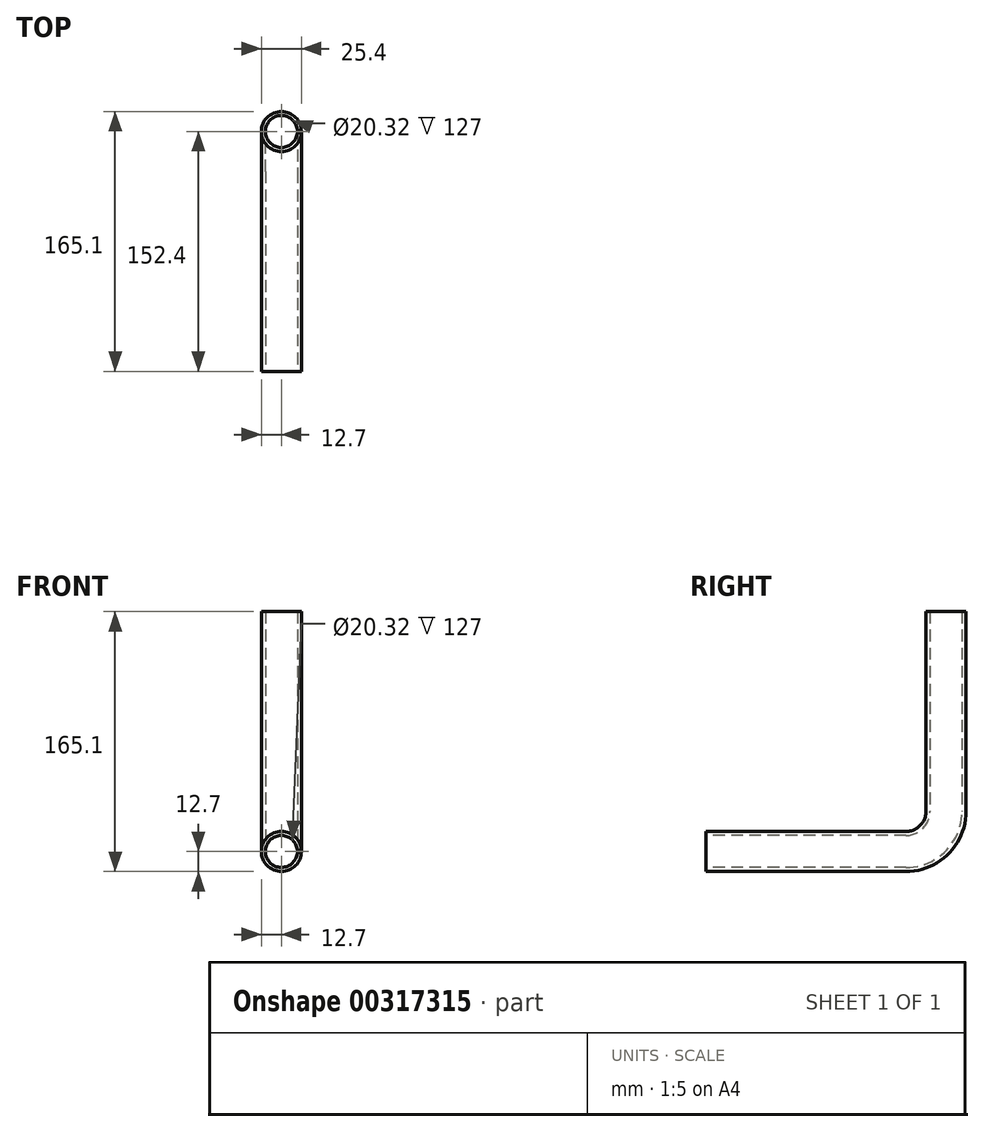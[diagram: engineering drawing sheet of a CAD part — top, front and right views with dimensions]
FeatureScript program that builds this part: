
annotation { "Feature Type Name" : "Feature", "Feature Type Description" : "" }
export const myFeature = defineFeature(function(context is Context, id is Id, definition is map)
    precondition{}
    {
        {
            var Q0;
            Q0=qCreatedBy(makeId("Right.planeOp"),FACE);
            var sketch = newSketch(context, id + "F0", { "sketchPlane" : qUnion([Q0])});
            skArc(sketch, "E0", {"start": v(-25.4, -152.4) * mm, "mid": v(-7.44, -144.96) * mm, "end": v(0, -127) * mm});
            skLineSegment(sketch, "E1", {"start": v(0, 0) * mm, "end": v(0, -127) * mm});
            skLineSegment(sketch, "E2", {"start": v(-25.4, -152.4) * mm, "end": v(-152.4, -152.4) * mm});
            skSolve(sketch);
        }
        {
            var Q0;
            Q0=qCreatedBy(makeId("Top.planeOp"),FACE);
            var sketch = newSketch(context, id + "F1", { "sketchPlane" : qUnion([Q0])});
            skCircle(sketch, "E3", {"center": v(0, 0) * mm, "radius": 12.7 * mm});
            skCircle(sketch, "E4", {"center": v(0, 0) * mm, "radius": 10.16 * mm});
            skSolve(sketch);
        }
        {
            var Q0;
            Q0=makeQuery(id+"F1.imprint","IMPRINT",FACE,{"disambiguationData":[TD([[makeQuery(id+"F1.imprint","IMPRINT",EDGE,{"derivedFrom":sQuery(id+"F1.wireOp",EDGE,"E3")}),1.0]])]});
            var Q1;
            Q1=sQuery(id+"F0.wireOp",EDGE,"E1");
            var Q2;
            Q2=sQuery(id+"F0.wireOp",EDGE,"E0");
            var Q3;
            Q3=sQuery(id+"F0.wireOp",EDGE,"E2");
            sweep(context, id + "F2", {"profiles" : qUnion([Q0]), "path" : qUnion([Q1, Q2, Q3])});
        }
    });
